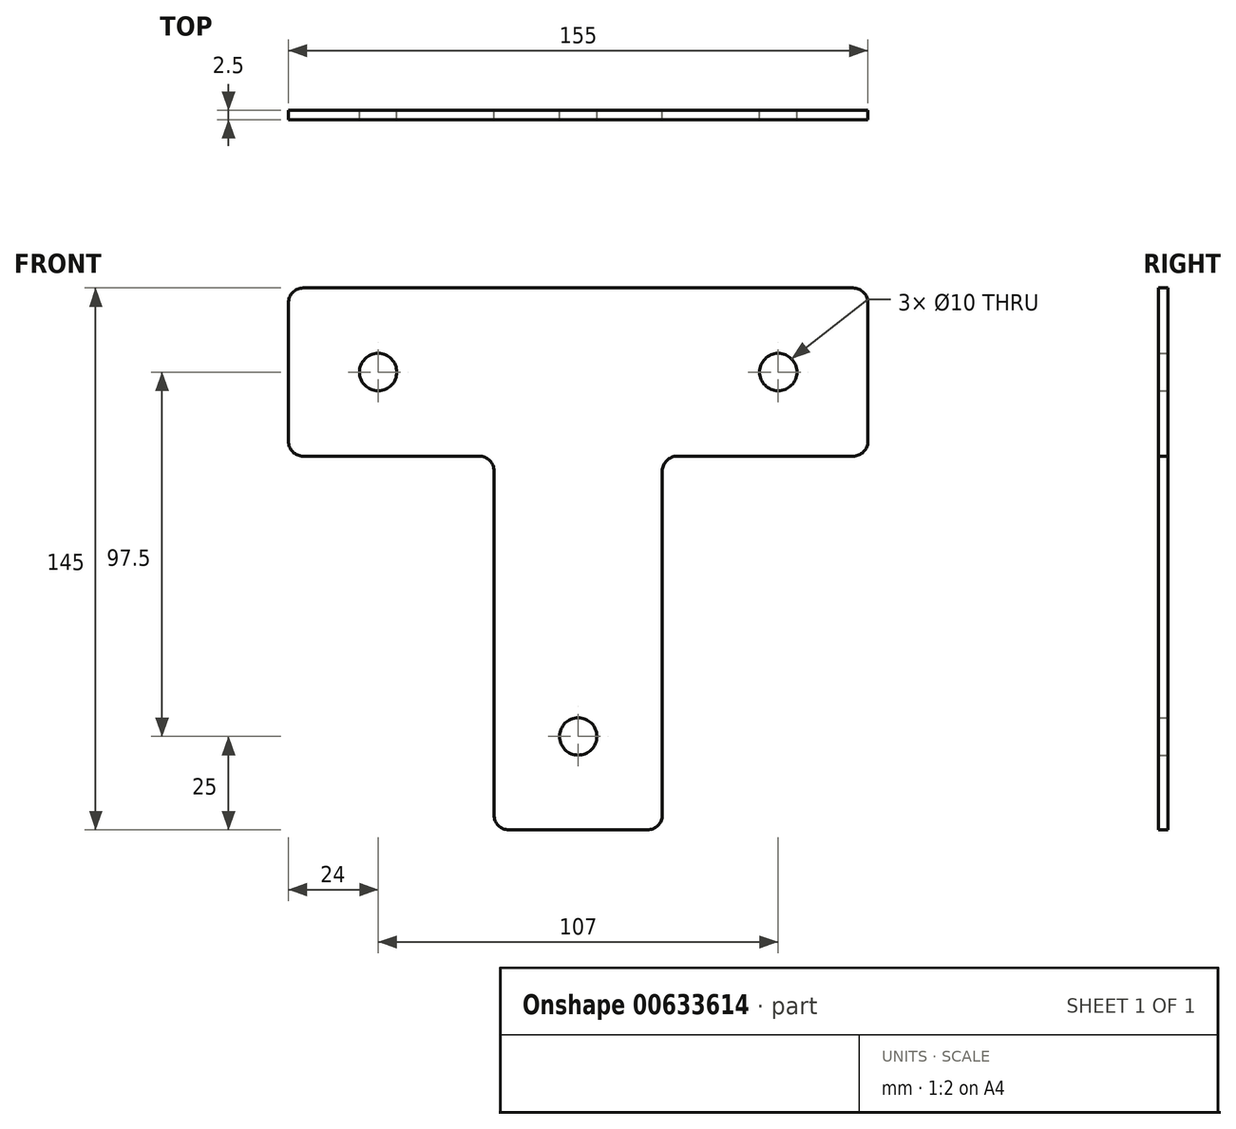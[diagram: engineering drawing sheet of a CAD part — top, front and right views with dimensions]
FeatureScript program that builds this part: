
annotation { "Feature Type Name" : "Feature", "Feature Type Description" : "" }
export const myFeature = defineFeature(function(context is Context, id is Id, definition is map)
    precondition{}
    {
        {
            var Q0;
            Q0=qCreatedBy(makeId("Front.planeOp"),FACE);
            var sketch = newSketch(context, id + "F0", { "sketchPlane" : qUnion([Q0])});
            skLineSegment(sketch, "E0.bottom", {"start": v(73.5, 22.5) * mm, "end": v(-73.5, 22.5) * mm});
            skLineSegment(sketch, "E0.top", {"start": v(77.5, -22.5) * mm, "end": v(-77.5, -22.5) * mm});
            skLineSegment(sketch, "E0.left", {"start": v(77.5, 18.5) * mm, "end": v(77.5, -18.5) * mm});
            skLineSegment(sketch, "E0.right", {"start": v(-77.5, 18.5) * mm, "end": v(-77.5, -18.5) * mm});
            skPoint(sketch, "E0.middle", {"position": v(0, 0) * mm});
            skLineSegment(sketch, "E1", {"start": v(77.5, -22.5) * mm, "end": v(22.5, -22.5) * mm});
            skLineSegment(sketch, "E2", {"start": v(26.5, -22.5) * mm, "end": v(73.5, -22.5) * mm});
            skLineSegment(sketch, "E3", {"start": v(18.5, -122.5) * mm, "end": v(-18.5, -122.5) * mm});
            skLineSegment(sketch, "E4", {"start": v(-22.5, -118.5) * mm, "end": v(-22.5, -26.5) * mm});
            skLineSegment(sketch, "E5", {"start": v(-26.5, -22.5) * mm, "end": v(-73.5, -22.5) * mm});
            skLineSegment(sketch, "E6", {"start": v(22.5, -26.5) * mm, "end": v(22.5, -118.5) * mm});
            skCircle(sketch, "E7", {"center": v(-53.5, 0) * mm, "radius": 5 * mm});
            skCircle(sketch, "E8", {"center": v(53.5, 0) * mm, "radius": 5 * mm});
            skCircle(sketch, "E9", {"center": v(0, -97.5) * mm, "radius": 5 * mm});
            skPoint(sketch, "E10.visualSharp", {"position": v(-77.5, 22.5) * mm});
            skArc(sketch, "E10.filletArc", {"start": v(-73.5, 22.5) * mm, "mid": v(-76.33, 21.33) * mm, "end": v(-77.5, 18.5) * mm});
            skPoint(sketch, "E11.visualSharp", {"position": v(77.5, 22.5) * mm});
            skArc(sketch, "E11.filletArc", {"start": v(77.5, 18.5) * mm, "mid": v(76.33, 21.33) * mm, "end": v(73.5, 22.5) * mm});
            skPoint(sketch, "E12.visualSharp", {"position": v(-77.5, -22.5) * mm});
            skArc(sketch, "E12.filletArc", {"start": v(-77.5, -18.5) * mm, "mid": v(-76.33, -21.33) * mm, "end": v(-73.5, -22.5) * mm});
            skPoint(sketch, "E13.visualSharp", {"position": v(77.5, -22.5) * mm});
            skArc(sketch, "E13.filletArc", {"start": v(73.5, -22.5) * mm, "mid": v(76.33, -21.33) * mm, "end": v(77.5, -18.5) * mm});
            skPoint(sketch, "E14.visualSharp", {"position": v(22.5, -22.5) * mm});
            skArc(sketch, "E14.filletArc", {"start": v(26.5, -22.5) * mm, "mid": v(23.67, -23.67) * mm, "end": v(22.5, -26.5) * mm});
            skPoint(sketch, "E15.visualSharp", {"position": v(-22.5, -22.5) * mm});
            skArc(sketch, "E15.filletArc", {"start": v(-22.5, -26.5) * mm, "mid": v(-23.67, -23.67) * mm, "end": v(-26.5, -22.5) * mm});
            skPoint(sketch, "E16.visualSharp", {"position": v(-22.5, -122.5) * mm});
            skArc(sketch, "E16.filletArc", {"start": v(-22.5, -118.5) * mm, "mid": v(-21.33, -121.33) * mm, "end": v(-18.5, -122.5) * mm});
            skPoint(sketch, "E17.visualSharp", {"position": v(22.5, -122.5) * mm});
            skArc(sketch, "E17.filletArc", {"start": v(18.5, -122.5) * mm, "mid": v(21.33, -121.33) * mm, "end": v(22.5, -118.5) * mm});
            skSolve(sketch);
        }
        {
            var Q0;
            Q0 = qSketchRegion(id + "F0", true);
            extrude(context, id + "F1", {"entities" : qUnion([Q0]), "depth" : 2.5 * mm, "offsetDistance" : 25 * mm});
        }
    });
